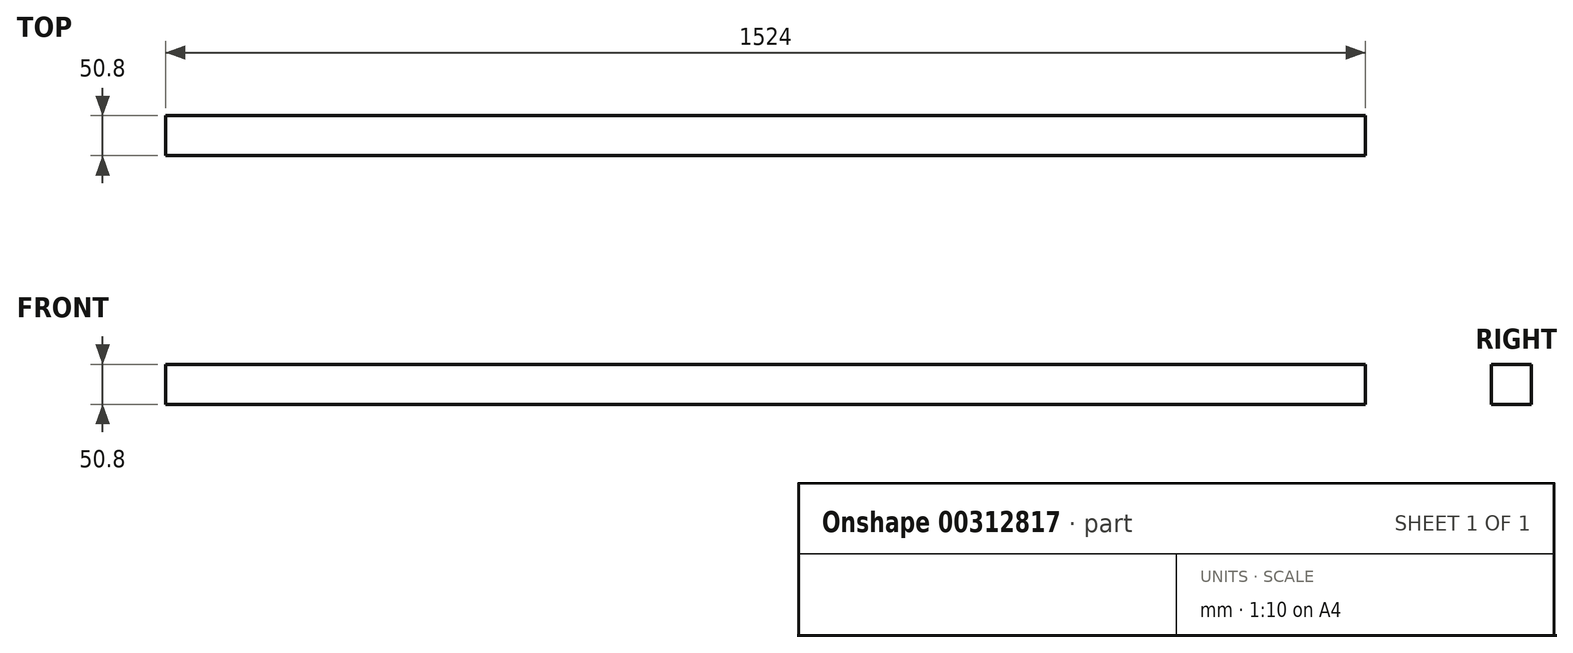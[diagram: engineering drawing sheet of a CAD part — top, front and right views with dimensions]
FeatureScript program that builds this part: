
annotation { "Feature Type Name" : "Feature", "Feature Type Description" : "" }
export const myFeature = defineFeature(function(context is Context, id is Id, definition is map)
    precondition{}
    {
        {
            var Q0;
            Q0=qCreatedBy(makeId("Front.planeOp"),FACE);
            var sketch = newSketch(context, id + "F0", { "sketchPlane" : qUnion([Q0])});
            skLineSegment(sketch, "E0.bottom", {"start": v(-767, 30.95) * mm, "end": v(757, 30.95) * mm});
            skLineSegment(sketch, "E0.top", {"start": v(-767, -19.85) * mm, "end": v(757, -19.85) * mm});
            skLineSegment(sketch, "E0.left", {"start": v(-767, 30.95) * mm, "end": v(-767, -19.85) * mm});
            skLineSegment(sketch, "E0.right", {"start": v(757, 30.95) * mm, "end": v(757, -19.85) * mm});
            skSolve(sketch);
        }
        {
            var Q0;
            Q0=makeQuery(id+"F0.imprint","IMPRINT",FACE,{"disambiguationData":[TD([[makeQuery(id+"F0.imprint","IMPRINT",EDGE,{"derivedFrom":sQuery(id+"F0.wireOp",EDGE,"E0.bottom")}),-1.0]])]});
            extrude(context, id + "F1", {"entities" : qUnion([Q0]), "depth" : 50.8 * mm});
        }
    });
